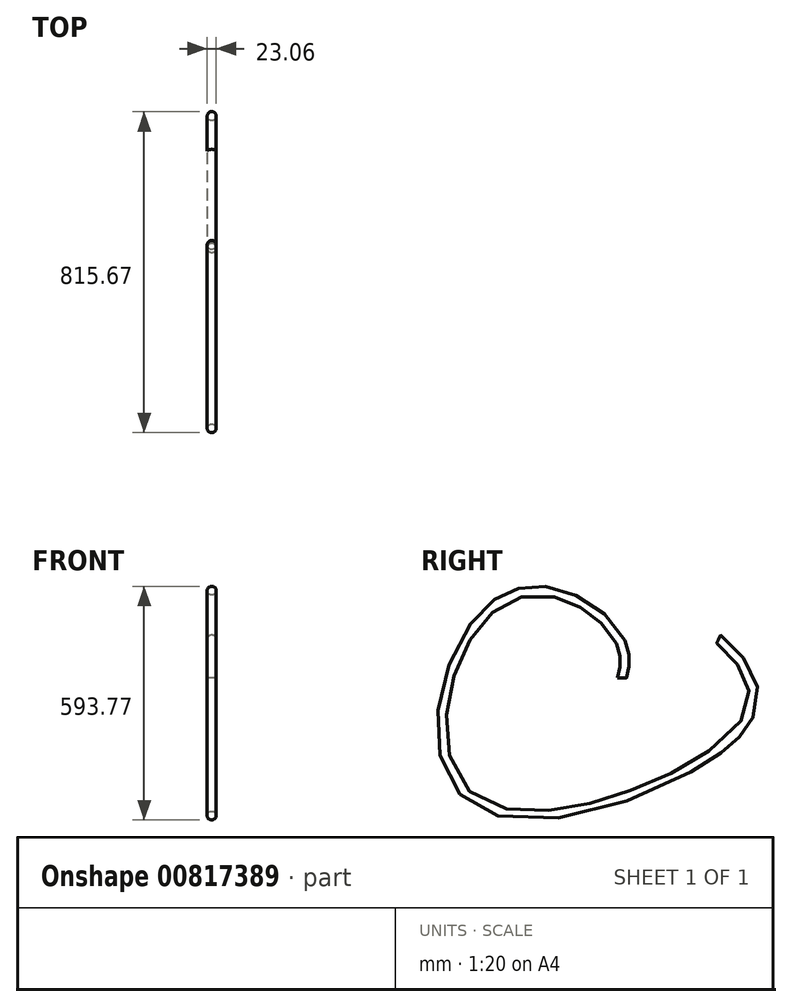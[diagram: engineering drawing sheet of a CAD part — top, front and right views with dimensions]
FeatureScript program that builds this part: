
annotation { "Feature Type Name" : "Feature", "Feature Type Description" : "" }
export const myFeature = defineFeature(function(context is Context, id is Id, definition is map)
    precondition{}
    {
        {
            var Q0;
            Q0=qCreatedBy(makeId("Right.planeOp"),FACE);
            var sketch = newSketch(context, id + "F0", { "sketchPlane" : qUnion([Q0])});
            skFitSpline(sketch, "E0", {"points": [v(0, 0) * mm, v(0, 74.29) * mm, v(-209.77, 149.28) * mm, v(-287.1, -259.12) * mm, v(324.29, -82.71) * mm, v(280.8, 42.95) * mm], "startDerivative": vector(227.2, 638.95) * mm, "endDerivative": vector(-797.4, 790.18) * mm});
            skArc(sketch, "E1", {"start": v(280.8, 59.36) * mm, "mid": v(276.6, 51.16) * mm, "end": v(280.8, 42.95) * mm});
            skSolve(sketch);
        }
        {
            var Q0;
            Q0=qCreatedBy(makeId("Top.planeOp"),FACE);
            var sketch = newSketch(context, id + "F1", { "sketchPlane" : qUnion([Q0])});
            skCircle(sketch, "E2", {"center": v(-48.98, 61.13) * mm, "radius": 11.53 * mm});
            skSolve(sketch);
        }
        {
            var Q0;
            Q0=makeQuery(id+"F1.imprint","IMPRINT",FACE,{"disambiguationData":[TD([[makeQuery(id+"F1.imprint","IMPRINT",EDGE,{"derivedFrom":sQuery(id+"F1.wireOp",EDGE,"E2")}),1.0]])]});
            var Q1;
            Q1=sQuery(id+"F0.wireOp",EDGE,"E0");
            sweep(context, id + "F2", {"profiles" : qUnion([Q0]), "path" : qUnion([Q1])});
        }
    });
